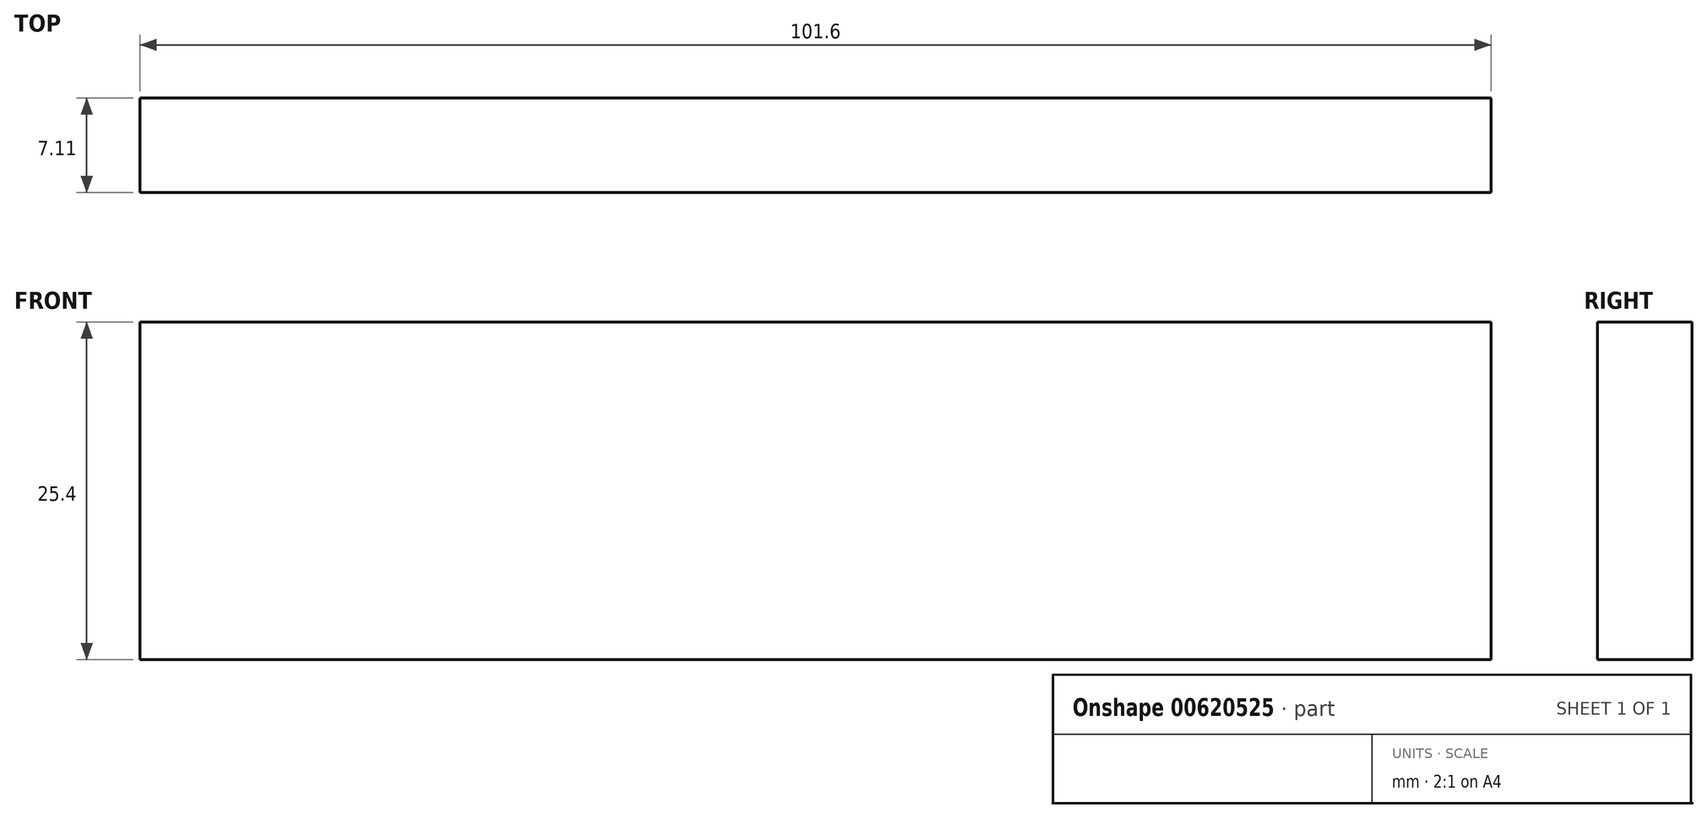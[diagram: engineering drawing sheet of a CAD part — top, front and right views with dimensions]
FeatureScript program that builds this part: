
annotation { "Feature Type Name" : "Feature", "Feature Type Description" : "" }
export const myFeature = defineFeature(function(context is Context, id is Id, definition is map)
    precondition{}
    {
        {
            var Q0;
            Q0=qCreatedBy(makeId("Front.planeOp"),FACE);
            var sketch = newSketch(context, id + "F0", { "sketchPlane" : qUnion([Q0])});
            skLineSegment(sketch, "E0.bottom", {"start": v(-52.25, 53.13) * mm, "end": v(49.35, 53.13) * mm});
            skLineSegment(sketch, "E0.top", {"start": v(-52.25, 27.73) * mm, "end": v(49.35, 27.73) * mm});
            skLineSegment(sketch, "E0.left", {"start": v(-52.25, 53.13) * mm, "end": v(-52.25, 27.73) * mm});
            skLineSegment(sketch, "E0.right", {"start": v(49.35, 53.13) * mm, "end": v(49.35, 27.73) * mm});
            skSolve(sketch);
        }
        {
            var Q0;
            Q0 = qSketchRegion(id + "F0", true);
            extrude(context, id + "F1", {"entities" : qUnion([Q0]), "depth" : 7.11 * mm, "offsetDistance" : 25.4 * mm});
        }
    });
